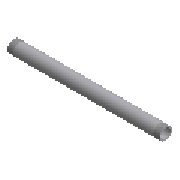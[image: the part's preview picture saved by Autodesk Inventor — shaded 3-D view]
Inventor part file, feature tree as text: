
AUTODESK INVENTOR PART (.ipt)
format: ipt  version: 2025 (Build 290162000, 162)  size: 167,424 bytes
history: native  units: mm (DEFAULTED — no unit token found)
features: other x8, revolve x1
ambient origin geometry x8: Origin, YZ Plane, XZ Plane, XY Plane, X Axis, Y Axis, Z Axis, Center Point
bodies: Solid1 (feature_tree)
feature tree (9):
  revolve  "Revolution1"  [1 undecoded]
  other  "Work Axis1"
  other  "Work Point5"
  other  "Work Axis2"
  other  "Work Point6"
  other  "Work Axis3"
  other  "Work Axis4"
  other  "Work Point7"
  other  "Work Point8"
note: 1 required parameter value undecoded (feature->parameter linkage not recoverable at this tier; creation-order binding heuristic only, values carry confidence <= 0.55)
